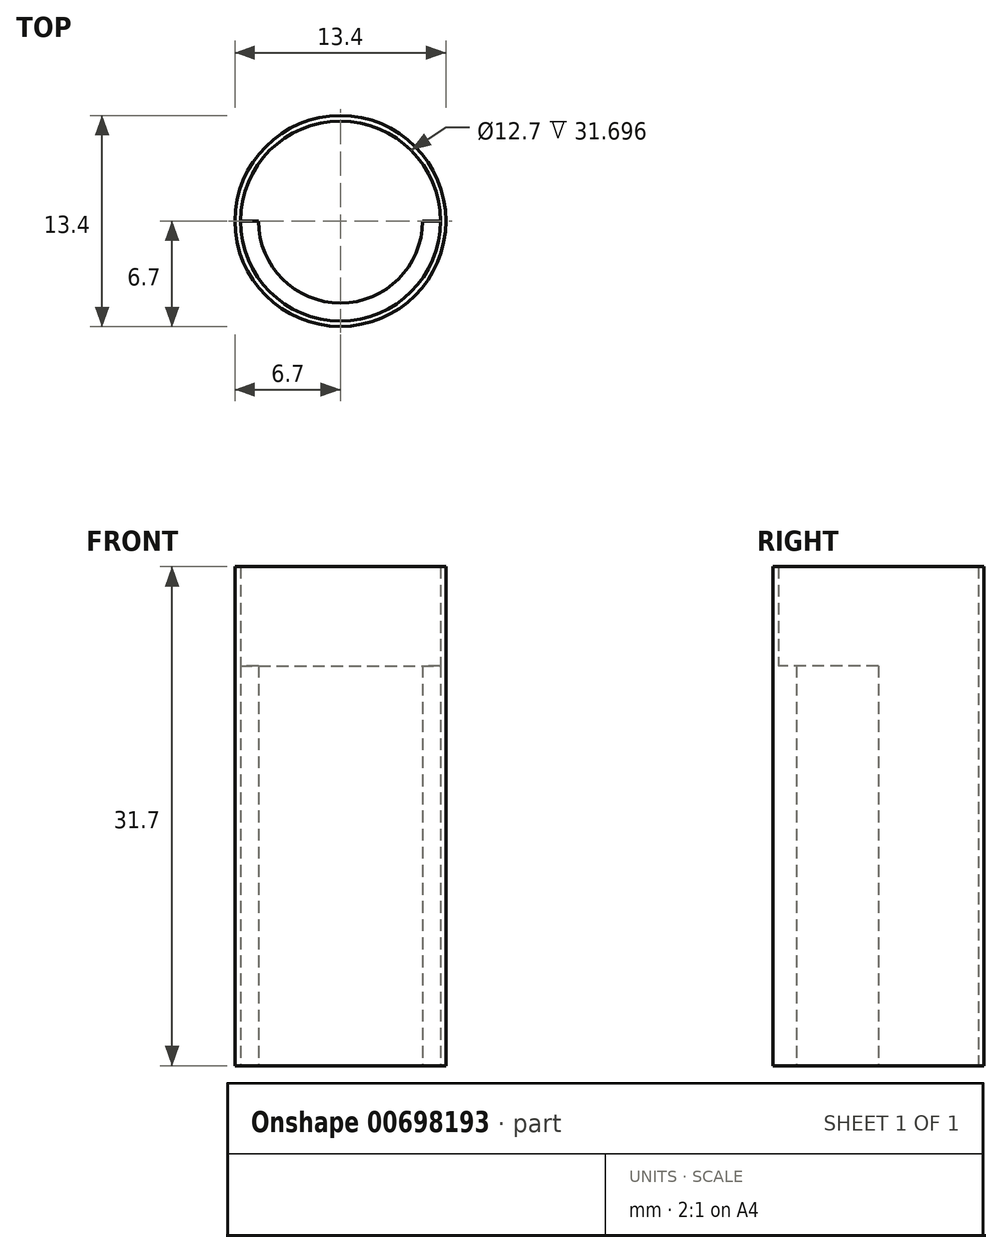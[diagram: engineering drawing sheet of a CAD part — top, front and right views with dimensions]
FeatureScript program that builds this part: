
annotation { "Feature Type Name" : "Feature", "Feature Type Description" : "" }
export const myFeature = defineFeature(function(context is Context, id is Id, definition is map)
    precondition{}
    {
        {
            var Q0;
            Q0=qCreatedBy(makeId("Top.planeOp"),FACE);
            var sketch = newSketch(context, id + "F0", { "sketchPlane" : qUnion([Q0])});
            skCircle(sketch, "E0", {"center": v(0, 0) * mm, "radius": 5.2 * mm});
            skCircle(sketch, "E1", {"center": v(0, 0) * mm, "radius": 6.35 * mm});
            skCircle(sketch, "E2", {"center": v(0, 0) * mm, "radius": 6.7 * mm});
            skLineSegment(sketch, "E3", {"start": v(6.35, 0) * mm, "end": v(5.2, 0) * mm});
            skLineSegment(sketch, "E4", {"start": v(-5.2, 0) * mm, "end": v(-6.35, 0) * mm});
            skSolve(sketch);
        }
        {
            var Q0;
            {var subQ0=sQuery(id+"F0.wireOp",EDGE,"E3");Q0=makeQuery(id+"F0.imprint","IMPRINT",FACE,{"disambiguationData":[TD([[makeQuery(id+"F0.imprint","IMPRINT",EDGE,{"derivedFrom":subQ0}),1.0]])]});}
            extrude(context, id + "F1", {"entities" : qUnion([Q0]), "depth" : 25.4 * mm, "offsetDistance" : 25.4 * mm});
        }
        {
            var Q0;
            Q0=makeQuery(id+"F0.imprint","IMPRINT",FACE,{"disambiguationData":[TD([[makeQuery(id+"F0.imprint","IMPRINT",EDGE,{"derivedFrom":sQuery(id+"F0.wireOp",EDGE,"E2")}),1.0]])]});
            extrude(context, id + "F2", {"entities" : qUnion([Q0]), "operationType" : NewBodyOperationType.ADD, "endBound" : BoundingType.THROUGH_ALL, "depth" : 25.4 * mm, "offsetDistance" : 25.4 * mm});
        }
    });
